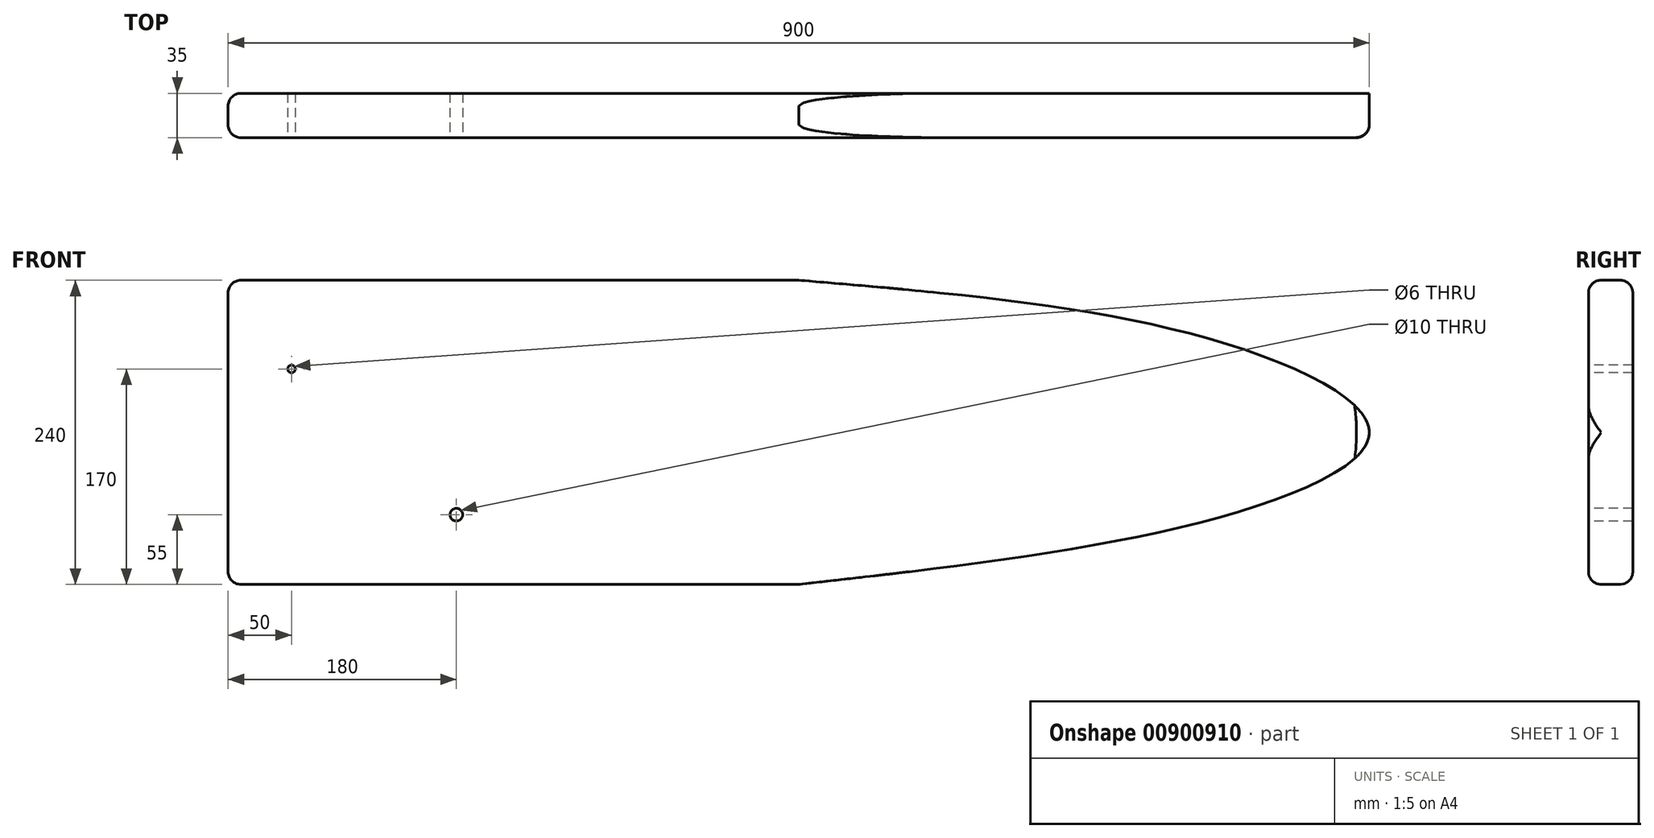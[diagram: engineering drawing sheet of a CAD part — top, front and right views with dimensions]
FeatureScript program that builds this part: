
annotation { "Feature Type Name" : "Feature", "Feature Type Description" : "" }
export const myFeature = defineFeature(function(context is Context, id is Id, definition is map)
    precondition{}
    {
        {
            var Q0;
            Q0=qCreatedBy(makeId("Front.planeOp"),FACE);
            var sketch = newSketch(context, id + "F0", { "sketchPlane" : qUnion([Q0])});
            skLineSegment(sketch, "E0.bottom", {"start": v(401.54, 120) * mm, "end": v(-450, 120) * mm});
            skLineSegment(sketch, "E0.top", {"start": v(401.54, -120) * mm, "end": v(-450, -120) * mm});
            skLineSegment(sketch, "E0.left", {"start": v(450, 0) * mm, "end": v(450, -0.18) * mm});
            skLineSegment(sketch, "E0.right", {"start": v(-450, 120) * mm, "end": v(-450, -120) * mm});
            skPoint(sketch, "E0.middle", {"position": v(0, 0) * mm});
            skFitSpline(sketch, "E1", {"points": [v(0, -120) * mm, v(344.74, -63.4) * mm, v(450, 0) * mm, v(336.81, 70) * mm, v(0, 120) * mm], "startDerivative": vector(1188.85, 133) * mm, "endDerivative": vector(-1163.14, 97.62) * mm});
            skEllipticalArc(sketch, "E2.trimOffspring", {});
            skPoint(sketch, "E3.orphan", {"position": v(450, 120) * mm});
            skPoint(sketch, "E4.orphan", {"position": v(450, -120) * mm});
            const initialGuessF0  = {"E2.trimOffspring": [0, 0, 1, 0, 0.45, 0.265830337013489, 5.814834002117591, 0.4683513050619536]};
            skSetInitialGuess(sketch, initialGuessF0);
            skSolve(sketch);
        }
        {
            var Q0;
            {var subQ5=sQuery(id+"F0.wireOp",EDGE,"E0.right");Q0=makeQuery(id+"F0.imprint","IMPRINT",FACE,{"disambiguationData":[TD([[makeQuery(id+"F0.imprint","IMPRINT",EDGE,{"derivedFrom":subQ5}),1.0]])]});}
            extrude(context, id + "F1", {"entities" : qUnion([Q0]), "depth" : 35 * mm, "offsetDistance" : 25 * mm});
        }
        {
            var Q0;
            Q0=makeQuery(id+"F1.opExtrude","CAP_FACE",FACE,{"disambiguationData":[OSD([sQuery(id+"F0.wireOp",EDGE,"E0.bottom"),sQuery(id+"F0.wireOp",EDGE,"E0.top"),sQuery(id+"F0.wireOp",EDGE,"E0.right"),sQuery(id+"F0.wireOp",EDGE,"E1")])],"isStart":false});
            var sketch = newSketch(context, id + "F2", { "sketchPlane" : qUnion([Q0])});
            skLineSegment(sketch, "E5", {"start": v(-450, 0) * mm, "end": v(0, 0) * mm});
            skLineSegment(sketch, "E6", {"start": v(-450, 50) * mm, "end": v(-265.07, 50) * mm});
            skCircle(sketch, "E7", {"center": v(-400, 50) * mm, "radius": 3 * mm});
            skCircle(sketch, "E8", {"center": v(-270, -65) * mm, "radius": 5 * mm});
            skSolve(sketch);
        }
        {
            var Q0;
            Q0 = qSketchRegion(id + "F2", true);
            extrude(context, id + "F3", {"entities" : qUnion([Q0]), "operationType" : NewBodyOperationType.REMOVE, "oppositeDirection" : true, "depth" : 100 * mm, "offsetDistance" : 25 * mm});
        }
        {
            var Q0;
            Q0=makeQuery(id+"F1.opExtrude","CAP_EDGE",EDGE,{"disambiguationData":[OSD([sQuery(id+"F0.wireOp",EDGE,"E0.bottom")])],"isStart":false});
            var Q1;
            Q1=makeQuery(id+"F1.opExtrude","CAP_EDGE",EDGE,{"disambiguationData":[OSD([sQuery(id+"F0.wireOp",EDGE,"E0.bottom")])],"isStart":true});
            var Q2;
            Q2=makeQuery(id+"F1.opExtrude","CAP_EDGE",EDGE,{"disambiguationData":[OSD([sQuery(id+"F0.wireOp",EDGE,"E0.top")])],"isStart":false});
            var Q3;
            Q3=makeQuery(id+"F1.opExtrude","CAP_EDGE",EDGE,{"disambiguationData":[OSD([sQuery(id+"F0.wireOp",EDGE,"E0.top")])],"isStart":true});
            fillet(context, id + "F4", {"entities" : qUnion([Q0, Q1, Q2, Q3]), "radius" : 10 * mm, "tangentPropagation" : true, "allowEdgeOverflow" : false});
        }
        {
            var Q0;
            Q0=makeQuery(id+"F1.opExtrude","CAP_EDGE",EDGE,{"disambiguationData":[OSD([sQuery(id+"F0.wireOp",EDGE,"E0.right")])],"isStart":false});
            var Q1;
            Q1=makeQuery(id+"F1.opExtrude","CAP_EDGE",EDGE,{"disambiguationData":[OSD([sQuery(id+"F0.wireOp",EDGE,"E2.trimOffspring")])],"isStart":false});
            fillet(context, id + "F5", {"entities" : qUnion([Q0, Q1]), "radius" : 10 * mm, "tangentPropagation" : true, "allowEdgeOverflow" : false});
        }
    });
